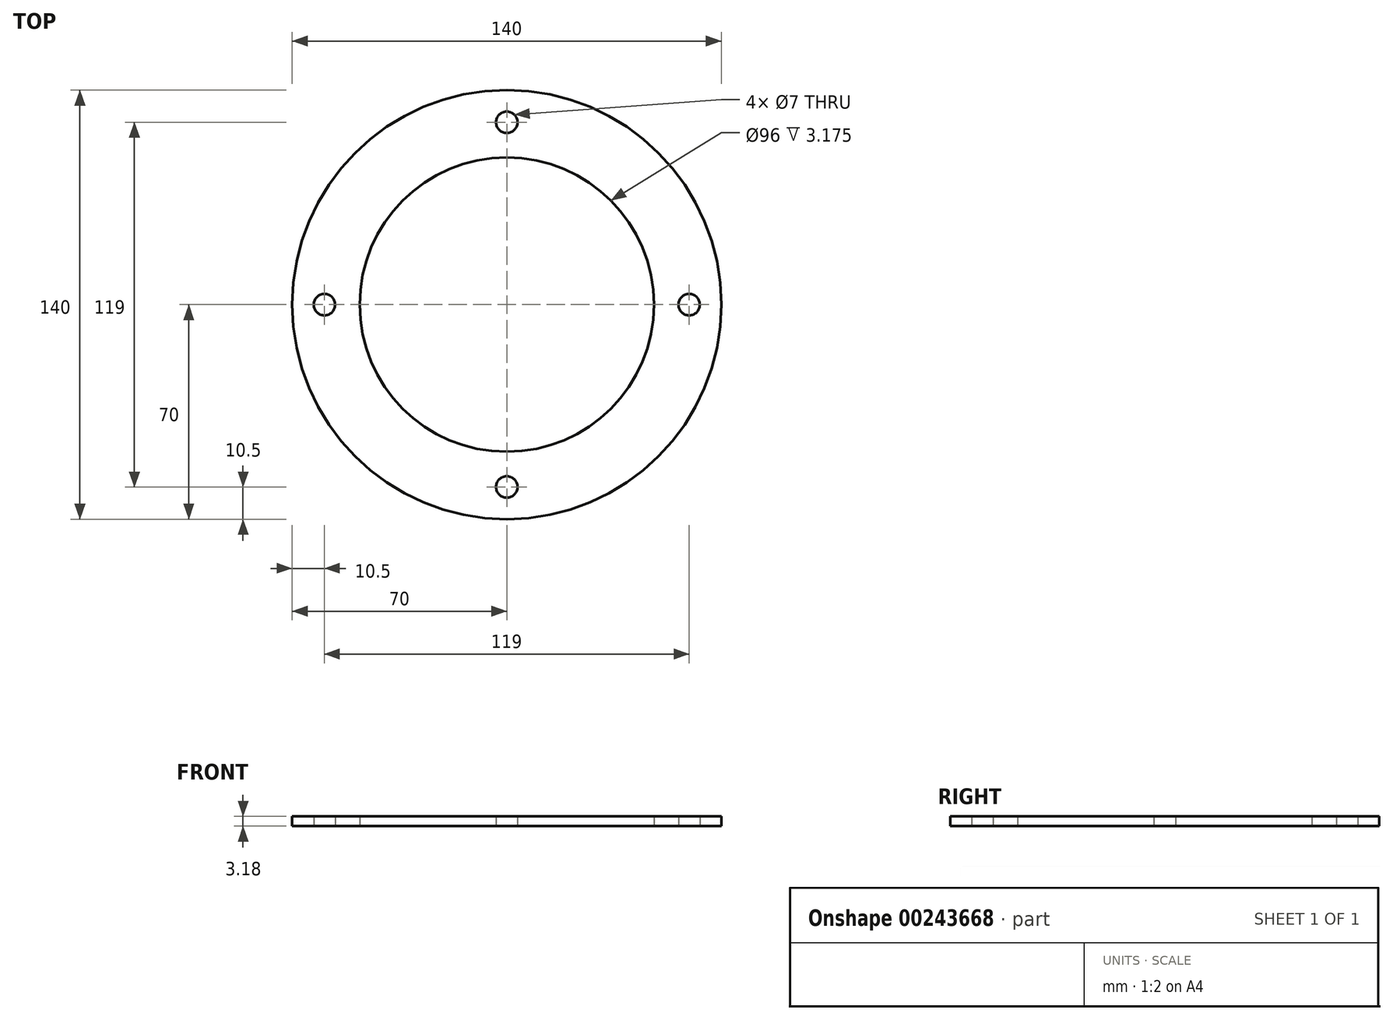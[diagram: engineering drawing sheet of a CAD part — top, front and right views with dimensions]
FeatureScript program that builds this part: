
annotation { "Feature Type Name" : "Feature", "Feature Type Description" : "" }
export const myFeature = defineFeature(function(context is Context, id is Id, definition is map)
    precondition{}
    {
        {
            var Q0;
            Q0=qCreatedBy(makeId("Top.planeOp"),FACE);
            var sketch = newSketch(context, id + "F0", { "sketchPlane" : qUnion([Q0])});
            skCircle(sketch, "E0", {"center": v(0, 0) * mm, "radius": 70 * mm});
            skLineSegment(sketch, "E1", {"start": v(0, 0) * mm, "end": v(0, 59.5) * mm, "construction": true});
            skLineSegment(sketch, "E2", {"start": v(0, 0) * mm, "end": v(59.5, 0) * mm, "construction": true});
            skLineSegment(sketch, "E3", {"start": v(0, 0) * mm, "end": v(-59.5, 0) * mm, "construction": true});
            skLineSegment(sketch, "E4", {"start": v(0, 0) * mm, "end": v(0, -59.5) * mm, "construction": true});
            skCircle(sketch, "E5", {"center": v(0, 59.5) * mm, "radius": 3.5 * mm});
            skCircle(sketch, "E6", {"center": v(59.5, 0) * mm, "radius": 3.5 * mm});
            skCircle(sketch, "E7", {"center": v(0, -59.5) * mm, "radius": 3.5 * mm});
            skCircle(sketch, "E8", {"center": v(-59.5, 0) * mm, "radius": 3.5 * mm});
            skCircle(sketch, "E9", {"center": v(0, 0) * mm, "radius": 48 * mm});
            skSolve(sketch);
        }
        {
            var Q0;
            Q0=qSketchRegion(id+"F0",true);
            extrude(context, id + "F1", {"entities" : qUnion([Q0]), "endBound" : BoundingType.SYMMETRIC, "depth" : 3.17 * mm});
        }
    });
